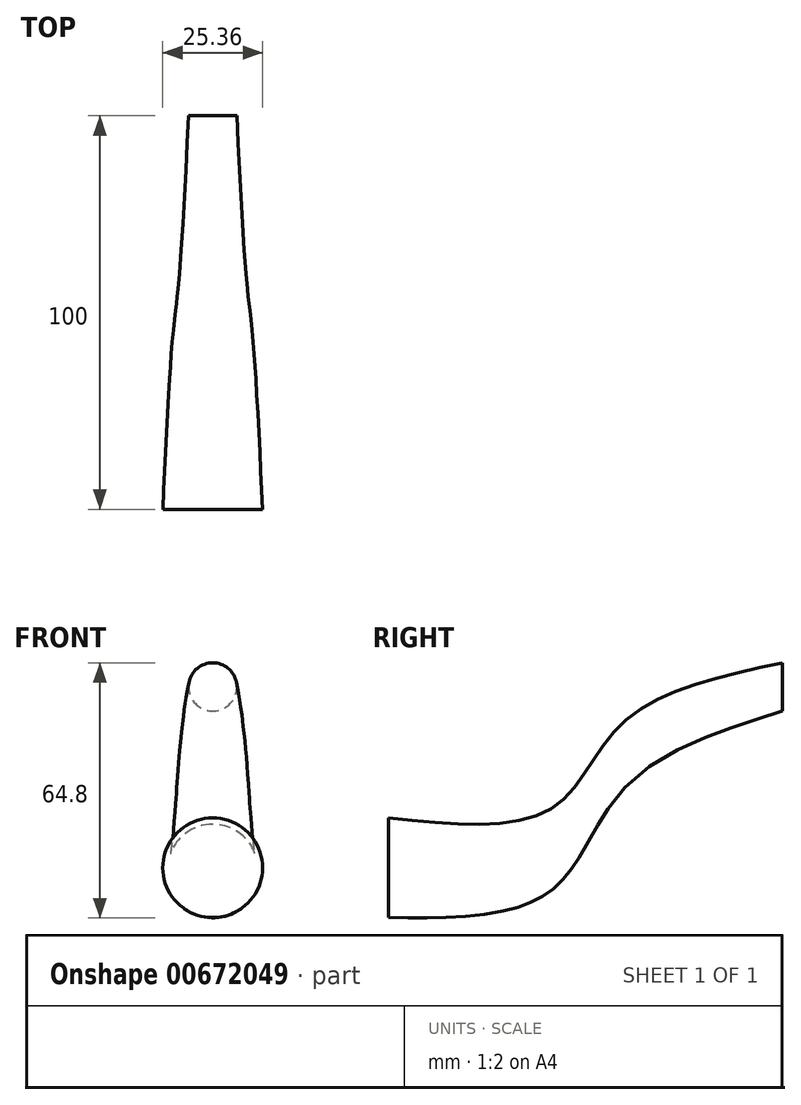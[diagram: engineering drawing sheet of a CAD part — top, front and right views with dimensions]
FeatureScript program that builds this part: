
annotation { "Feature Type Name" : "Feature", "Feature Type Description" : "" }
export const myFeature = defineFeature(function(context is Context, id is Id, definition is map)
    precondition{}
    {
        {
            var Q0;
            Q0=qCreatedBy(makeId("Front.planeOp"),FACE);
            var sketch = newSketch(context, id + "F0", { "sketchPlane" : qUnion([Q0])});
            skCircle(sketch, "E0", {"center": v(0, 0) * mm, "radius": 12.68 * mm});
            skSolve(sketch);
        }
        {
            var Q0;
            Q0=qCreatedBy(makeId("Front.planeOp"),FACE);
            cPlane(context, id + "F1", {"entities" : qUnion([Q0]), "cplaneType" : CPlaneType.OFFSET, "offset" : 100 * mm, "oppositeDirection" : true, "width" : 150 * mm, "height" : 150 * mm});
        }
        {
            var Q0;
            Q0=qCreatedBy(id+"F1.planeOp",FACE);
            var sketch = newSketch(context, id + "F2", { "sketchPlane" : qUnion([Q0])});
            skCircle(sketch, "E1", {"center": v(0, 45.94) * mm, "radius": 6.13 * mm});
            skSolve(sketch);
        }
        {
            var Q0;
            Q0=qCreatedBy(makeId("Right.planeOp"),FACE);
            var sketch = newSketch(context, id + "F3", { "sketchPlane" : qUnion([Q0])});
            skLineSegment(sketch, "E2.0", {"start": v(0, -12.68) * mm, "end": v(0, 12.68) * mm});
            skLineSegment(sketch, "E3.0", {"start": v(100, 39.8) * mm, "end": v(100, 52.07) * mm});
            skFitSpline(sketch, "E4", {"points": [v(100, 52.07) * mm, v(59.53, 36.85) * mm, v(41.53, 15.16) * mm, v(0, 12.68) * mm], "startDerivative": vector(-131.3, -28.51) * mm, "endDerivative": vector(-137.48, 14.63) * mm});
            skSolve(sketch);
        }
        {
            var Q0;
            Q0=makeQuery(id+"F2.imprint","IMPRINT",FACE,{"disambiguationData":[TD([[makeQuery(id+"F2.imprint","IMPRINT",EDGE,{"derivedFrom":sQuery(id+"F2.wireOp",EDGE,"E1")}),1.0]])]});
            var Q1;
            Q1=makeQuery(id+"F0.imprint","IMPRINT",FACE,{"disambiguationData":[TD([[makeQuery(id+"F0.imprint","IMPRINT",EDGE,{"derivedFrom":sQuery(id+"F0.wireOp",EDGE,"E0")}),1.0]])]});
            var Q2;
            Q2=sQuery(id+"F3.wireOp",EDGE,"E4");
            loft(context, id + "F4", {"addGuides" : true, "sheetProfilesArray" : [{ "sheetProfileEntities" : qUnion([Q0]) }, { "sheetProfileEntities" : qUnion([Q1]) }], "guidesArray" : [{ "guideEntities" : qUnion([Q2]), "guideDerivativeType" : LoftGuideDerivativeType.DEFAULT, "guideDerivativeMagnitude" : 1 }]});
        }
    });
